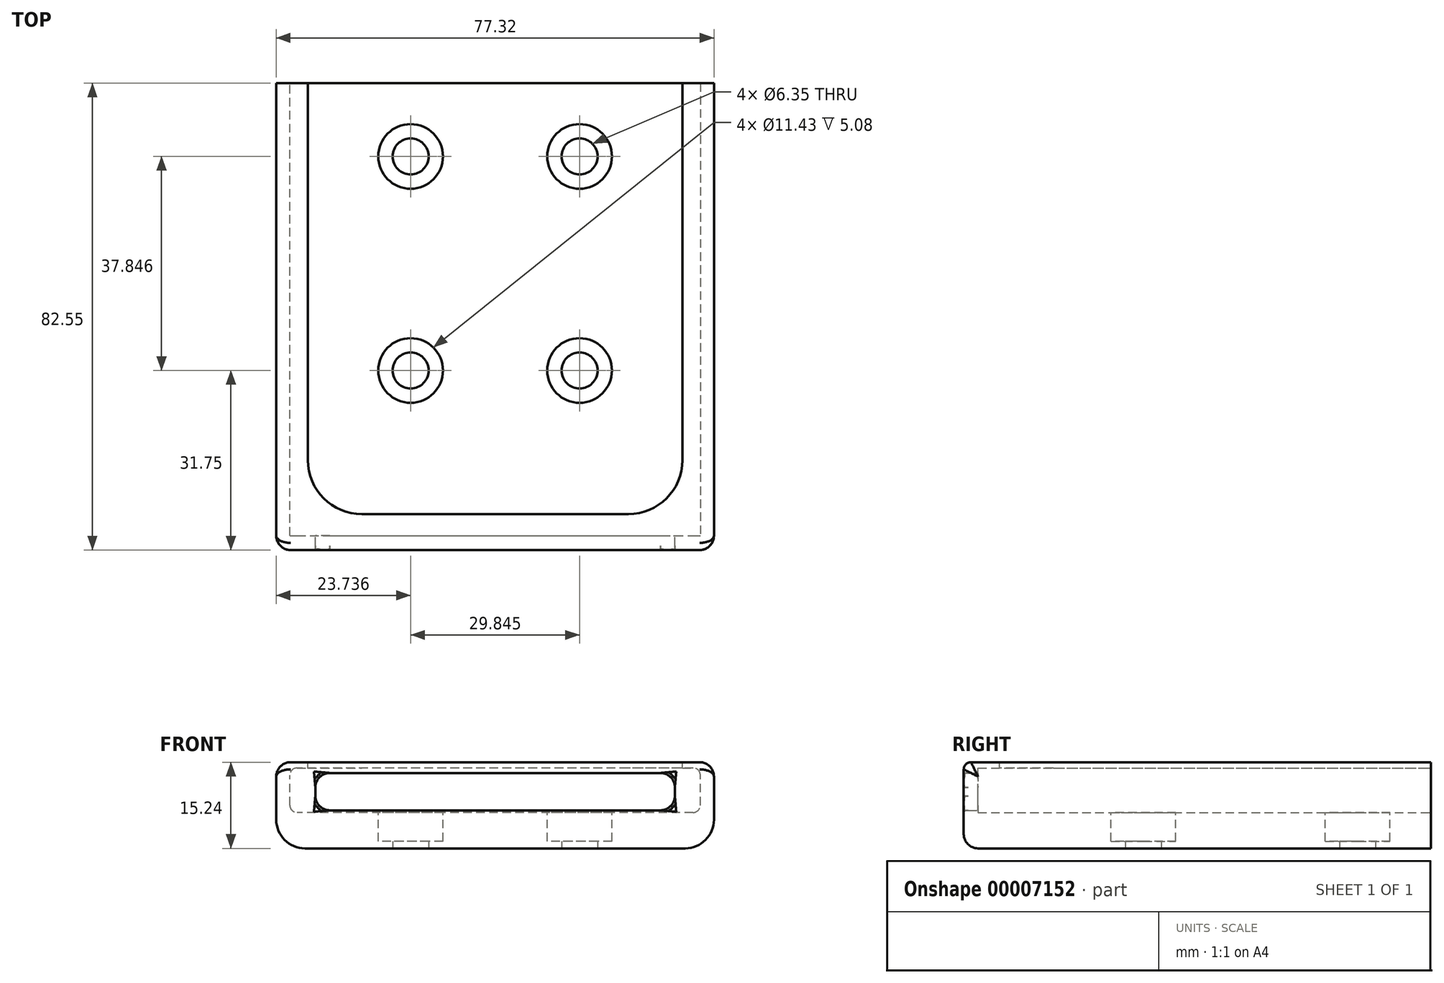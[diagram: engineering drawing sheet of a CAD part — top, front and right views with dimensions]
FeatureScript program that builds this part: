
annotation { "Feature Type Name" : "Feature", "Feature Type Description" : "" }
export const myFeature = defineFeature(function(context is Context, id is Id, definition is map)
    precondition{}
    {
        {
            var Q0;
            Q0=qCreatedBy(makeId("Top.planeOp"),FACE);
            var sketch = newSketch(context, id + "F0", { "sketchPlane" : qUnion([Q0])});
            skLineSegment(sketch, "E0.bottom", {"start": v(0, 0) * mm, "end": v(77.32, 0) * mm});
            skLineSegment(sketch, "E0.top", {"start": v(0, 146.05) * mm, "end": v(77.32, 146.05) * mm});
            skLineSegment(sketch, "E0.left", {"start": v(0, 0) * mm, "end": v(0, 146.05) * mm});
            skLineSegment(sketch, "E0.right", {"start": v(77.32, 0) * mm, "end": v(77.32, 146.05) * mm});
            skSolve(sketch);
        }
        {
            var Q0;
            Q0 = qSketchRegion(id + "F0", true);
            extrude(context, id + "F1", {"entities" : qUnion([Q0]), "depth" : 15.24 * mm});
        }
        {
            var Q0;
            Q0=makeQuery(id+"F1.opExtrude","CAP_FACE",FACE,{"disambiguationData":[OSD([sQuery(id+"F0.wireOp",EDGE,"E0.bottom"),sQuery(id+"F0.wireOp",EDGE,"E0.top"),sQuery(id+"F0.wireOp",EDGE,"E0.left"),sQuery(id+"F0.wireOp",EDGE,"E0.right")])],"isStart":false});
            var sketch = newSketch(context, id + "F2", { "sketchPlane" : qUnion([Q0])});
            skLineSegment(sketch, "E1.bottom", {"start": v(5.59, 6.35) * mm, "end": v(71.73, 6.35) * mm});
            skLineSegment(sketch, "E1.top", {"start": v(5.59, 146.05) * mm, "end": v(71.73, 146.05) * mm});
            skLineSegment(sketch, "E1.left", {"start": v(5.59, 6.35) * mm, "end": v(5.59, 146.05) * mm});
            skLineSegment(sketch, "E1.right", {"start": v(71.73, 6.35) * mm, "end": v(71.73, 146.05) * mm});
            skLineSegment(sketch, "E2", {"start": v(38.66, 6.35) * mm, "end": v(38.66, 93.9) * mm, "construction": true});
            skLineSegment(sketch, "E3", {"start": v(38.66, 0) * mm, "end": v(38.66, 53.26) * mm, "construction": true});
            skSolve(sketch);
        }
        {
            var Q0;
            Q0 = qSketchRegion(id + "F2", true);
            extrude(context, id + "F3", {"entities" : qUnion([Q0]), "operationType" : NewBodyOperationType.REMOVE, "oppositeDirection" : true, "depth" : 8.9 * mm});
        }
        {
            var Q0;
            Q0=makeQuery(id+"F3.boolean.opBoolean","COPY",FACE,{"derivedFrom":makeQuery(id+"F3.opExtrude","SWEPT_FACE",FACE,{"disambiguationData":[OSD([sQuery(id+"F2.wireOp",EDGE,"E1.right")])]})});
            var sketch = newSketch(context, id + "F4", { "sketchPlane" : qUnion([Q0])});
            skLineSegment(sketch, "E4.bottom", {"start": v(-146.05, 6.35) * mm, "end": v(-6.35, 6.35) * mm});
            skLineSegment(sketch, "E4.top", {"start": v(-146.05, 14.22) * mm, "end": v(-6.35, 14.22) * mm});
            skLineSegment(sketch, "E4.left", {"start": v(-146.05, 6.35) * mm, "end": v(-146.05, 14.22) * mm});
            skLineSegment(sketch, "E4.right", {"start": v(-6.35, 6.35) * mm, "end": v(-6.35, 14.22) * mm});
            skSolve(sketch);
        }
        {
            var Q0;
            Q0=makeQuery(id+"F3.boolean.opBoolean","COPY",FACE,{"derivedFrom":makeQuery(id+"F3.opExtrude","SWEPT_FACE",FACE,{"disambiguationData":[OSD([sQuery(id+"F2.wireOp",EDGE,"E1.left")])]})});
            var sketch = newSketch(context, id + "F5", { "sketchPlane" : qUnion([Q0])});
            skLineSegment(sketch, "E5.bottom", {"start": v(6.35, 6.35) * mm, "end": v(146.05, 6.35) * mm});
            skLineSegment(sketch, "E5.top", {"start": v(6.35, 14.22) * mm, "end": v(146.05, 14.22) * mm});
            skLineSegment(sketch, "E5.left", {"start": v(6.35, 6.35) * mm, "end": v(6.35, 14.22) * mm});
            skLineSegment(sketch, "E5.right", {"start": v(146.05, 6.35) * mm, "end": v(146.05, 14.22) * mm});
            skSolve(sketch);
        }
        {
            var Q0;
            Q0=makeQuery(id+"F4.imprint","IMPRINT",FACE,{"disambiguationData":[TD([[makeQuery(id+"F4.imprint","IMPRINT",EDGE,{"derivedFrom":sQuery(id+"F4.wireOp",EDGE,"E4.bottom")}),-1.0]])]});
            var Q1;
            Q1=makeQuery(id+"F5.imprint","IMPRINT",FACE,{"disambiguationData":[TD([[makeQuery(id+"F5.imprint","IMPRINT",EDGE,{"derivedFrom":sQuery(id+"F5.wireOp",EDGE,"E5.bottom")}),1.0]])]});
            extrude(context, id + "F6", {"entities" : qUnion([Q0, Q1]), "operationType" : NewBodyOperationType.REMOVE, "endBound" : BoundingType.SYMMETRIC, "oppositeDirection" : true, "depth" : 6.35 * mm});
        }
        {
            var Q0;
            Q0=makeQuery(id+"F6.boolean.opBoolean","MERGE",FACE,{"derivedFrom":[makeQuery(id+"F3.boolean.opBoolean","COPY",FACE,{"derivedFrom":makeQuery(id+"F3.opExtrude","SWEPT_FACE",FACE,{"disambiguationData":[OSD([sQuery(id+"F2.wireOp",EDGE,"E1.bottom")])]})}),makeQuery(id+"F6.opExtrude","SWEPT_FACE",FACE,{"disambiguationData":[OSD([sQuery(id+"F4.wireOp",EDGE,"E4.right")])]}),makeQuery(id+"F6.opExtrude","SWEPT_FACE",FACE,{"disambiguationData":[OSD([sQuery(id+"F5.wireOp",EDGE,"E5.left")])]})]});
            var sketch = newSketch(context, id + "F7", { "sketchPlane" : qUnion([Q0])});
            skLineSegment(sketch, "E6.rect.bottom", {"start": v(-70.4, 13.33) * mm, "end": v(-6.9, 13.33) * mm});
            skLineSegment(sketch, "E6.rect.top", {"start": v(-70.4, 6.73) * mm, "end": v(-6.9, 6.73) * mm});
            skLineSegment(sketch, "E6.rect.left", {"start": v(-70.4, 13.33) * mm, "end": v(-70.4, 6.73) * mm});
            skLineSegment(sketch, "E6.rect.right", {"start": v(-6.9, 13.33) * mm, "end": v(-6.9, 6.73) * mm});
            skSolve(sketch);
        }
        {
            var Q0;
            Q0=makeQuery(id+"F7.imprint","IMPRINT",FACE,{"disambiguationData":[TD([[makeQuery(id+"F7.imprint","IMPRINT",EDGE,{"derivedFrom":sQuery(id+"F7.wireOp",EDGE,"E6.rect.bottom")}),-1.0]])]});
            extrude(context, id + "F8", {"entities" : qUnion([Q0]), "operationType" : NewBodyOperationType.REMOVE, "oppositeDirection" : true, "depth" : 7.62 * mm});
        }
        {
            var Q0;
            Q0=makeQuery(id+"F1.opExtrude","CAP_EDGE",EDGE,{"disambiguationData":[OSD([sQuery(id+"F0.wireOp",EDGE,"E0.right")])],"isStart":true});
            var Q1;
            Q1=makeQuery(id+"F1.opExtrude","CAP_EDGE",EDGE,{"disambiguationData":[OSD([sQuery(id+"F0.wireOp",EDGE,"E0.left")])],"isStart":true});
            fillet(context, id + "F9", {"entities" : qUnion([Q0, Q1]), "radius" : 5.08 * mm, "tangentPropagation" : true, "allowEdgeOverflow" : false});
        }
        {
            var Q0;
            Q0=makeQuery(id+"F1.opExtrude","CAP_EDGE",EDGE,{"disambiguationData":[OSD([sQuery(id+"F0.wireOp",EDGE,"E0.bottom")])],"isStart":false});
            fillet(context, id + "F10", {"entities" : qUnion([Q0]), "radius" : 1.27 * mm, "tangentPropagation" : true, "allowEdgeOverflow" : false});
        }
        {
            var Q0;
            Q0=makeQuery(id+"F8.boolean.opBoolean","INTERSECT",EDGE,{"derivedFrom":[makeQuery(id+"F1.opExtrude","SWEPT_FACE",FACE,{"disambiguationData":[OSD([sQuery(id+"F0.wireOp",EDGE,"E0.bottom")])]}),makeQuery(id+"F8.opExtrude","SWEPT_FACE",FACE,{"disambiguationData":[OSD([sQuery(id+"F7.wireOp",EDGE,"E6.rect.bottom")])]})]});
            var Q1;
            Q1=makeQuery(id+"F8.boolean.opBoolean","INTERSECT",EDGE,{"derivedFrom":[makeQuery(id+"F1.opExtrude","SWEPT_FACE",FACE,{"disambiguationData":[OSD([sQuery(id+"F0.wireOp",EDGE,"E0.bottom")])]}),makeQuery(id+"F8.opExtrude","SWEPT_FACE",FACE,{"disambiguationData":[OSD([sQuery(id+"F7.wireOp",EDGE,"E6.rect.left")])]})]});
            var Q2;
            Q2=makeQuery(id+"F8.boolean.opBoolean","INTERSECT",EDGE,{"derivedFrom":[makeQuery(id+"F1.opExtrude","SWEPT_FACE",FACE,{"disambiguationData":[OSD([sQuery(id+"F0.wireOp",EDGE,"E0.bottom")])]}),makeQuery(id+"F8.opExtrude","SWEPT_FACE",FACE,{"disambiguationData":[OSD([sQuery(id+"F7.wireOp",EDGE,"E6.rect.top")])]})]});
            var Q3;
            Q3=makeQuery(id+"F8.boolean.opBoolean","INTERSECT",EDGE,{"derivedFrom":[makeQuery(id+"F1.opExtrude","SWEPT_FACE",FACE,{"disambiguationData":[OSD([sQuery(id+"F0.wireOp",EDGE,"E0.bottom")])]}),makeQuery(id+"F8.opExtrude","SWEPT_FACE",FACE,{"disambiguationData":[OSD([sQuery(id+"F7.wireOp",EDGE,"E6.rect.right")])]})]});
            fillet(context, id + "F11", {"entities" : qUnion([Q0, Q1, Q2, Q3]), "radius" : 0.25 * mm, "tangentPropagation" : true, "allowEdgeOverflow" : false});
        }
        {
            var Q0;
            Q0=makeQuery(id+"F3.boolean.opBoolean","COPY",EDGE,{"derivedFrom":makeQuery(id+"F3.opExtrude","SWEPT_EDGE",EDGE,{"disambiguationData":[OSD([sQuery(id+"F2.wireOp",EDGE,"E1.bottom"),sQuery(id+"F2.wireOp",EDGE,"E1.left")])]})});
            var Q1;
            Q1=makeQuery(id+"F3.boolean.opBoolean","COPY",EDGE,{"derivedFrom":makeQuery(id+"F3.opExtrude","SWEPT_EDGE",EDGE,{"disambiguationData":[OSD([sQuery(id+"F2.wireOp",EDGE,"E1.bottom"),sQuery(id+"F2.wireOp",EDGE,"E1.right")])]})});
            fillet(context, id + "F12", {"entities" : qUnion([Q0, Q1]), "radius" : 9.52 * mm, "tangentPropagation" : true, "defaultsChanged" : true, "vertexSettings" : [], "allowEdgeOverflow" : false});
        }
        {
            var Q0;
            Q0=makeQuery(id+"F1.opExtrude","CAP_FACE",FACE,{"disambiguationData":[OSD([sQuery(id+"F0.wireOp",EDGE,"E0.bottom"),sQuery(id+"F0.wireOp",EDGE,"E0.top"),sQuery(id+"F0.wireOp",EDGE,"E0.left"),sQuery(id+"F0.wireOp",EDGE,"E0.right")])],"isStart":true});
            var sketch = newSketch(context, id + "F13", { "sketchPlane" : qUnion([Q0])});
            skLineSegment(sketch, "E7", {"start": v(38.66, -146.05) * mm, "end": v(38.66, -31.46) * mm, "construction": true});
            skLineSegment(sketch, "E8.rect.bottom", {"start": v(23.74, -69.6) * mm, "end": v(53.58, -69.6) * mm, "construction": true});
            skLineSegment(sketch, "E8.rect.top", {"start": v(23.74, -31.75) * mm, "end": v(53.58, -31.75) * mm, "construction": true});
            skLineSegment(sketch, "E8.rect.left", {"start": v(23.74, -69.6) * mm, "end": v(23.74, -31.75) * mm, "construction": true});
            skLineSegment(sketch, "E8.rect.right", {"start": v(53.58, -69.6) * mm, "end": v(53.58, -31.75) * mm, "construction": true});
            skPoint(sketch, "E8.rect.middle", {"position": v(38.66, -50.67) * mm});
            skCircle(sketch, "E9", {"center": v(53.58, -69.6) * mm, "radius": 3.18 * mm});
            skCircle(sketch, "E10.0.MirrorC", {"center": v(23.74, -69.6) * mm, "radius": 3.18 * mm});
            skLineSegment(sketch, "E11", {"start": v(53.58, -50.67) * mm, "end": v(23.74, -50.67) * mm, "construction": true});
            skCircle(sketch, "E12.0.MirrorC", {"center": v(53.58, -31.75) * mm, "radius": 3.18 * mm});
            skCircle(sketch, "E12.1.MirrorC", {"center": v(23.74, -31.75) * mm, "radius": 3.18 * mm});
            skSolve(sketch);
        }
        {
            var Q0;
            Q0 = qSketchRegion(id + "F13", true);
            extrude(context, id + "F14", {"entities" : qUnion([Q0]), "operationType" : NewBodyOperationType.REMOVE, "oppositeDirection" : true, "depth" : 25.4 * mm});
        }
        {
            var Q0;
            Q0=makeQuery(id+"F8.boolean.opBoolean","MERGE",FACE,{"derivedFrom":[makeQuery(id+"F6.boolean.opBoolean","MERGE",FACE,{"derivedFrom":[makeQuery(id+"F3.boolean.opBoolean","COPY",FACE,{"derivedFrom":makeQuery(id+"F3.opExtrude","CAP_FACE",FACE,{"disambiguationData":[OSD([sQuery(id+"F2.wireOp",EDGE,"E1.bottom"),sQuery(id+"F2.wireOp",EDGE,"E1.top"),sQuery(id+"F2.wireOp",EDGE,"E1.left"),sQuery(id+"F2.wireOp",EDGE,"E1.right")])],"isStart":false})}),makeQuery(id+"F6.opExtrude","SWEPT_FACE",FACE,{"disambiguationData":[OSD([sQuery(id+"F4.wireOp",EDGE,"E4.bottom")])]}),makeQuery(id+"F6.opExtrude","SWEPT_FACE",FACE,{"disambiguationData":[OSD([sQuery(id+"F5.wireOp",EDGE,"E5.bottom")])]})]}),makeQuery(id+"F8.opExtrude","SWEPT_FACE",FACE,{"disambiguationData":[OSD([sQuery(id+"F7.wireOp",EDGE,"E6.rect.top")])]})]});
            var sketch = newSketch(context, id + "F15", { "sketchPlane" : qUnion([Q0])});
            skCircle(sketch, "E13", {"center": v(23.74, 69.6) * mm, "radius": 5.72 * mm});
            skLineSegment(sketch, "E14", {"start": v(23.74, 69.6) * mm, "end": v(53.58, 69.6) * mm, "construction": true});
            skLineSegment(sketch, "E15", {"start": v(53.58, 31.75) * mm, "end": v(23.74, 31.75) * mm, "construction": true});
            skLineSegment(sketch, "E16", {"start": v(23.74, 31.75) * mm, "end": v(23.74, 69.6) * mm, "construction": true});
            skLineSegment(sketch, "E17", {"start": v(53.58, 69.6) * mm, "end": v(53.58, 31.75) * mm, "construction": true});
            skLineSegment(sketch, "E18", {"start": v(53.58, 50.67) * mm, "end": v(23.74, 50.67) * mm, "construction": true});
            skLineSegment(sketch, "E19", {"start": v(23.74, 50.67) * mm, "end": v(38.66, 69.6) * mm, "construction": true});
            skLineSegment(sketch, "E20", {"start": v(38.66, 69.6) * mm, "end": v(38.66, 31.75) * mm, "construction": true});
            skCircle(sketch, "E21.0.MirrorC", {"center": v(23.74, 31.75) * mm, "radius": 5.72 * mm});
            skCircle(sketch, "E22.0.MirrorC", {"center": v(53.58, 69.6) * mm, "radius": 5.72 * mm});
            skCircle(sketch, "E22.1.MirrorC", {"center": v(53.58, 31.75) * mm, "radius": 5.72 * mm});
            skSolve(sketch);
        }
        {
            var Q0;
            Q0 = qSketchRegion(id + "F15", true);
            extrude(context, id + "F16", {"entities" : qUnion([Q0]), "operationType" : NewBodyOperationType.REMOVE, "oppositeDirection" : true, "depth" : 5.08 * mm});
        }
        {
            var Q0;
            Q0=makeQuery(id+"F6.boolean.opBoolean","MERGE",FACE,{"derivedFrom":[makeQuery(id+"F3.boolean.opBoolean","COPY",FACE,{"derivedFrom":makeQuery(id+"F3.opExtrude","SWEPT_FACE",FACE,{"disambiguationData":[OSD([sQuery(id+"F2.wireOp",EDGE,"E1.bottom")])]})}),makeQuery(id+"F6.opExtrude","SWEPT_FACE",FACE,{"disambiguationData":[OSD([sQuery(id+"F4.wireOp",EDGE,"E4.right")])]}),makeQuery(id+"F6.opExtrude","SWEPT_FACE",FACE,{"disambiguationData":[OSD([sQuery(id+"F5.wireOp",EDGE,"E5.left")])]})]});
            var sketch = newSketch(context, id + "F17", { "sketchPlane" : qUnion([Q0])});
            skLineSegment(sketch, "E23.bottom", {"start": v(-2.41, 6.35) * mm, "end": v(-74.9, 6.35) * mm});
            skLineSegment(sketch, "E23.top", {"start": v(-2.41, 14.22) * mm, "end": v(-74.9, 14.22) * mm});
            skLineSegment(sketch, "E23.left", {"start": v(-2.41, 6.35) * mm, "end": v(-2.41, 14.22) * mm});
            skLineSegment(sketch, "E23.right", {"start": v(-74.9, 6.35) * mm, "end": v(-74.9, 14.22) * mm});
            skSolve(sketch);
        }
        {
            var Q0;
            Q0 = qSketchRegion(id + "F17", true);
            extrude(context, id + "F18", {"entities" : qUnion([Q0]), "operationType" : NewBodyOperationType.REMOVE, "oppositeDirection" : true, "depth" : 3.8 * mm});
        }
        {
            var Q0;
            Q0=makeQuery(id+"F1.opExtrude","CAP_FACE",FACE,{"disambiguationData":[OSD([sQuery(id+"F0.wireOp",EDGE,"E0.bottom"),sQuery(id+"F0.wireOp",EDGE,"E0.top"),sQuery(id+"F0.wireOp",EDGE,"E0.left"),sQuery(id+"F0.wireOp",EDGE,"E0.right")])],"isStart":false});
            var sketch = newSketch(context, id + "F19", { "sketchPlane" : qUnion([Q0])});
            skLineSegment(sketch, "E24.bottom", {"start": v(77.32, 146.05) * mm, "end": v(0, 146.05) * mm});
            skLineSegment(sketch, "E24.top", {"start": v(77.32, 82.55) * mm, "end": v(0, 82.55) * mm});
            skLineSegment(sketch, "E24.left", {"start": v(77.32, 146.05) * mm, "end": v(77.32, 82.55) * mm});
            skLineSegment(sketch, "E24.right", {"start": v(0, 146.05) * mm, "end": v(0, 82.55) * mm});
            skSolve(sketch);
        }
        {
            var Q0;
            Q0 = qSketchRegion(id + "F19", true);
            extrude(context, id + "F20", {"entities" : qUnion([Q0]), "operationType" : NewBodyOperationType.REMOVE, "oppositeDirection" : true, "depth" : 25.4 * mm});
        }
        {
            var Q0;
            Q0=makeQuery(id+"F1.opExtrude","CAP_EDGE",EDGE,{"disambiguationData":[OSD([sQuery(id+"F0.wireOp",EDGE,"E0.left")])],"isStart":false});
            var Q1;
            Q1=makeQuery(id+"F1.opExtrude","CAP_EDGE",EDGE,{"disambiguationData":[OSD([sQuery(id+"F0.wireOp",EDGE,"E0.right")])],"isStart":false});
            fillet(context, id + "F21", {"entities" : qUnion([Q0, Q1]), "tangentPropagation" : true, "radius" : 2.54 * mm, "defaultsChanged" : true, "vertexSettings" : [], "allowEdgeOverflow" : false});
        }
        {
            var Q0;
            Q0=makeQuery(id+"F18.boolean.opBoolean","MERGE",EDGE,{"derivedFrom":[makeQuery(id+"F6.boolean.opBoolean","COPY",EDGE,{"derivedFrom":makeQuery(id+"F6.opExtrude","CAP_EDGE",EDGE,{"disambiguationData":[OSD([sQuery(id+"F4.wireOp",EDGE,"E4.bottom")])],"isStart":false})})],"fromTools":[makeQuery(id+"F18.opExtrude","SWEPT_EDGE",EDGE,{"disambiguationData":[OSD([sQuery(id+"F17.wireOp",EDGE,"E23.bottom"),sQuery(id+"F17.wireOp",EDGE,"E23.right")])]})]});
            var Q1;
            Q1=makeQuery(id+"F18.boolean.opBoolean","MERGE",EDGE,{"derivedFrom":[makeQuery(id+"F6.boolean.opBoolean","COPY",EDGE,{"derivedFrom":makeQuery(id+"F6.opExtrude","CAP_EDGE",EDGE,{"disambiguationData":[OSD([sQuery(id+"F5.wireOp",EDGE,"E5.bottom")])],"isStart":true})})],"fromTools":[makeQuery(id+"F18.opExtrude","SWEPT_EDGE",EDGE,{"disambiguationData":[OSD([sQuery(id+"F17.wireOp",EDGE,"E23.bottom"),sQuery(id+"F17.wireOp",EDGE,"E23.left")])]})]});
            var Q2;
            Q2=makeQuery(id+"F18.boolean.opBoolean","MERGE",EDGE,{"derivedFrom":[makeQuery(id+"F6.boolean.opBoolean","COPY",EDGE,{"derivedFrom":makeQuery(id+"F6.opExtrude","CAP_EDGE",EDGE,{"disambiguationData":[OSD([sQuery(id+"F4.wireOp",EDGE,"E4.top")])],"isStart":false})})],"fromTools":[makeQuery(id+"F18.opExtrude","SWEPT_EDGE",EDGE,{"disambiguationData":[OSD([sQuery(id+"F17.wireOp",EDGE,"E23.top"),sQuery(id+"F17.wireOp",EDGE,"E23.right")])]})]});
            var Q3;
            Q3=makeQuery(id+"F18.boolean.opBoolean","MERGE",EDGE,{"derivedFrom":[makeQuery(id+"F6.boolean.opBoolean","COPY",EDGE,{"derivedFrom":makeQuery(id+"F6.opExtrude","CAP_EDGE",EDGE,{"disambiguationData":[OSD([sQuery(id+"F5.wireOp",EDGE,"E5.top")])],"isStart":true})})],"fromTools":[makeQuery(id+"F18.opExtrude","SWEPT_EDGE",EDGE,{"disambiguationData":[OSD([sQuery(id+"F17.wireOp",EDGE,"E23.top"),sQuery(id+"F17.wireOp",EDGE,"E23.left")])]})]});
            fillet(context, id + "F22", {"entities" : qUnion([Q0, Q1, Q2, Q3]), "tangentPropagation" : true, "radius" : 1.27 * mm, "defaultsChanged" : true, "vertexSettings" : [], "allowEdgeOverflow" : false});
        }
        {
            var Q0;
            Q0=makeQuery(id+"F8.boolean.opBoolean","COPY",EDGE,{"derivedFrom":makeQuery(id+"F8.opExtrude","SWEPT_EDGE",EDGE,{"disambiguationData":[OSD([sQuery(id+"F7.wireOp",EDGE,"E6.rect.top"),sQuery(id+"F7.wireOp",EDGE,"E6.rect.left")])]})});
            var Q1;
            Q1=makeQuery(id+"F8.boolean.opBoolean","COPY",EDGE,{"derivedFrom":makeQuery(id+"F8.opExtrude","SWEPT_EDGE",EDGE,{"disambiguationData":[OSD([sQuery(id+"F7.wireOp",EDGE,"E6.rect.bottom"),sQuery(id+"F7.wireOp",EDGE,"E6.rect.left")])]})});
            var Q2;
            Q2=makeQuery(id+"F8.boolean.opBoolean","COPY",EDGE,{"derivedFrom":makeQuery(id+"F8.opExtrude","SWEPT_EDGE",EDGE,{"disambiguationData":[OSD([sQuery(id+"F7.wireOp",EDGE,"E6.rect.top"),sQuery(id+"F7.wireOp",EDGE,"E6.rect.right")])]})});
            var Q3;
            Q3=makeQuery(id+"F8.boolean.opBoolean","COPY",EDGE,{"derivedFrom":makeQuery(id+"F8.opExtrude","SWEPT_EDGE",EDGE,{"disambiguationData":[OSD([sQuery(id+"F7.wireOp",EDGE,"E6.rect.bottom"),sQuery(id+"F7.wireOp",EDGE,"E6.rect.right")])]})});
            fillet(context, id + "F23", {"entities" : qUnion([Q0, Q1, Q2, Q3]), "radius" : 2.54 * mm, "allowEdgeOverflow" : false});
        }
    });
